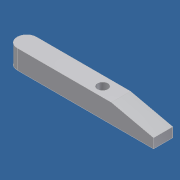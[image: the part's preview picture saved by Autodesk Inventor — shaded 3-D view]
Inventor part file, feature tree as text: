
AUTODESK INVENTOR PART (.ipt)
format: ipt  version: unknown  size: 189,952 bytes
history: native  units: in
note: dims shown in document units (in); Inventor stores cm internally (conversion verified against a paired STEP export)
features: sketch x3, hole x2, extrude x1, fillet x1
ambient origin geometry x8: Origin, YZ Plane, XZ Plane, XY Plane, X Axis, Y Axis, Z Axis, Center Point
bodies: Solid1 (feature_tree)
feature tree (7):
  extrude  "Extrusion1"  Depth=4.75in
  hole  "Hole1"  [1 undecoded]
  hole  "Hole2"  [1 undecoded]
  fillet  "Fillet1"  Radius=0.3125in
  sketch  "Sketch1"  dims[d0=0.313in d1=4.75in]
  sketch  "Sketch2"  dims[d3=1.375in d5=0.3125in]
  sketch  "Sketch3"  dims[d6=0.625in d7=0.0in d8=1.968in d9=0.3125in d10=0.343in d11=0.75in d12=0.375in d13=0.25in d14=0.5635in d15=1.0in d16=0.0in d17=2.282in d18=0.3125in d19=0.266in d20=0.75in d21=0.375in d22=0.25in d23=0.5635in d24=0.25in d25=0.0in d30=0.313in]
note: 2 required parameter values undecoded (feature->parameter linkage not recoverable at this tier; creation-order binding heuristic only, values carry confidence <= 0.55)
